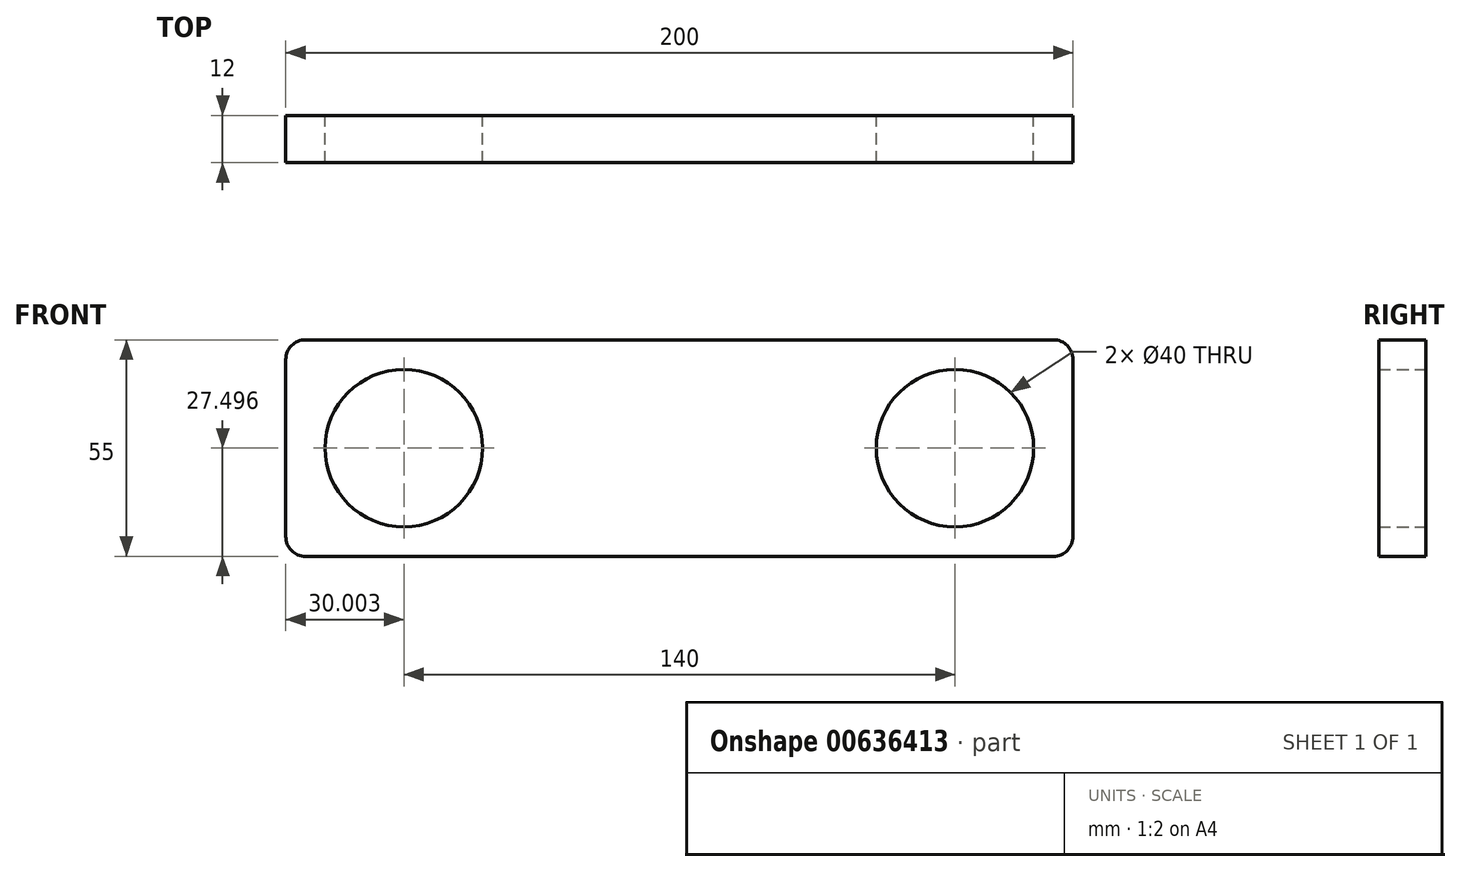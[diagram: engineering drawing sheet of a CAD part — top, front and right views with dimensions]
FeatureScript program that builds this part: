
annotation { "Feature Type Name" : "Feature", "Feature Type Description" : "" }
export const myFeature = defineFeature(function(context is Context, id is Id, definition is map)
    precondition{}
    {
        {
            var Q0;
            Q0=qCreatedBy(makeId("Front.planeOp"),FACE);
            var sketch = newSketch(context, id + "F0", { "sketchPlane" : qUnion([Q0])});
            skLineSegment(sketch, "E0.bottom", {"start": v(-79.88, 47.92) * mm, "end": v(110.12, 47.92) * mm});
            skLineSegment(sketch, "E0.top", {"start": v(-79.88, -7.08) * mm, "end": v(110.12, -7.08) * mm});
            skLineSegment(sketch, "E0.left", {"start": v(-84.88, 42.92) * mm, "end": v(-84.88, -2.08) * mm});
            skLineSegment(sketch, "E0.right", {"start": v(115.12, 42.92) * mm, "end": v(115.12, -2.08) * mm});
            skPoint(sketch, "E1.visualSharp", {"position": v(-84.88, 47.92) * mm});
            skArc(sketch, "E1.filletArc", {"start": v(-79.88, 47.92) * mm, "mid": v(-83.41, 46.45) * mm, "end": v(-84.88, 42.92) * mm});
            skPoint(sketch, "E2.visualSharp", {"position": v(115.12, 47.92) * mm});
            skArc(sketch, "E2.filletArc", {"start": v(115.12, 42.92) * mm, "mid": v(113.66, 46.45) * mm, "end": v(110.12, 47.92) * mm});
            skPoint(sketch, "E3.visualSharp", {"position": v(115.12, -7.08) * mm});
            skArc(sketch, "E3.filletArc", {"start": v(110.12, -7.08) * mm, "mid": v(113.66, -5.62) * mm, "end": v(115.12, -2.08) * mm});
            skPoint(sketch, "E4.visualSharp", {"position": v(-84.88, -7.08) * mm});
            skArc(sketch, "E4.filletArc", {"start": v(-84.88, -2.08) * mm, "mid": v(-83.41, -5.62) * mm, "end": v(-79.88, -7.08) * mm});
            skCircle(sketch, "E5", {"center": v(-54.88, 20.42) * mm, "radius": 20 * mm});
            skCircle(sketch, "E6.MirrorC", {"center": v(285.12, 20.42) * mm, "radius": 20 * mm});
            skLineSegment(sketch, "E7.MirrorCS", {"start": v(315.12, 42.92) * mm, "end": v(315.12, -2.08) * mm});
            skCircle(sketch, "E8", {"center": v(85.12, 20.42) * mm, "radius": 20 * mm});
            skSolve(sketch);
        }
        {
            var Q0;
            Q0=makeQuery(id+"F0.imprint","IMPRINT",FACE,{"disambiguationData":[TD([[makeQuery(id+"F0.imprint","IMPRINT",EDGE,{"derivedFrom":sQuery(id+"F0.wireOp",EDGE,"E0.bottom")}),-1.0]])]});
            extrude(context, id + "F1", {"entities" : qUnion([Q0]), "depth" : 12 * mm, "offsetDistance" : 25 * mm});
        }
    });
